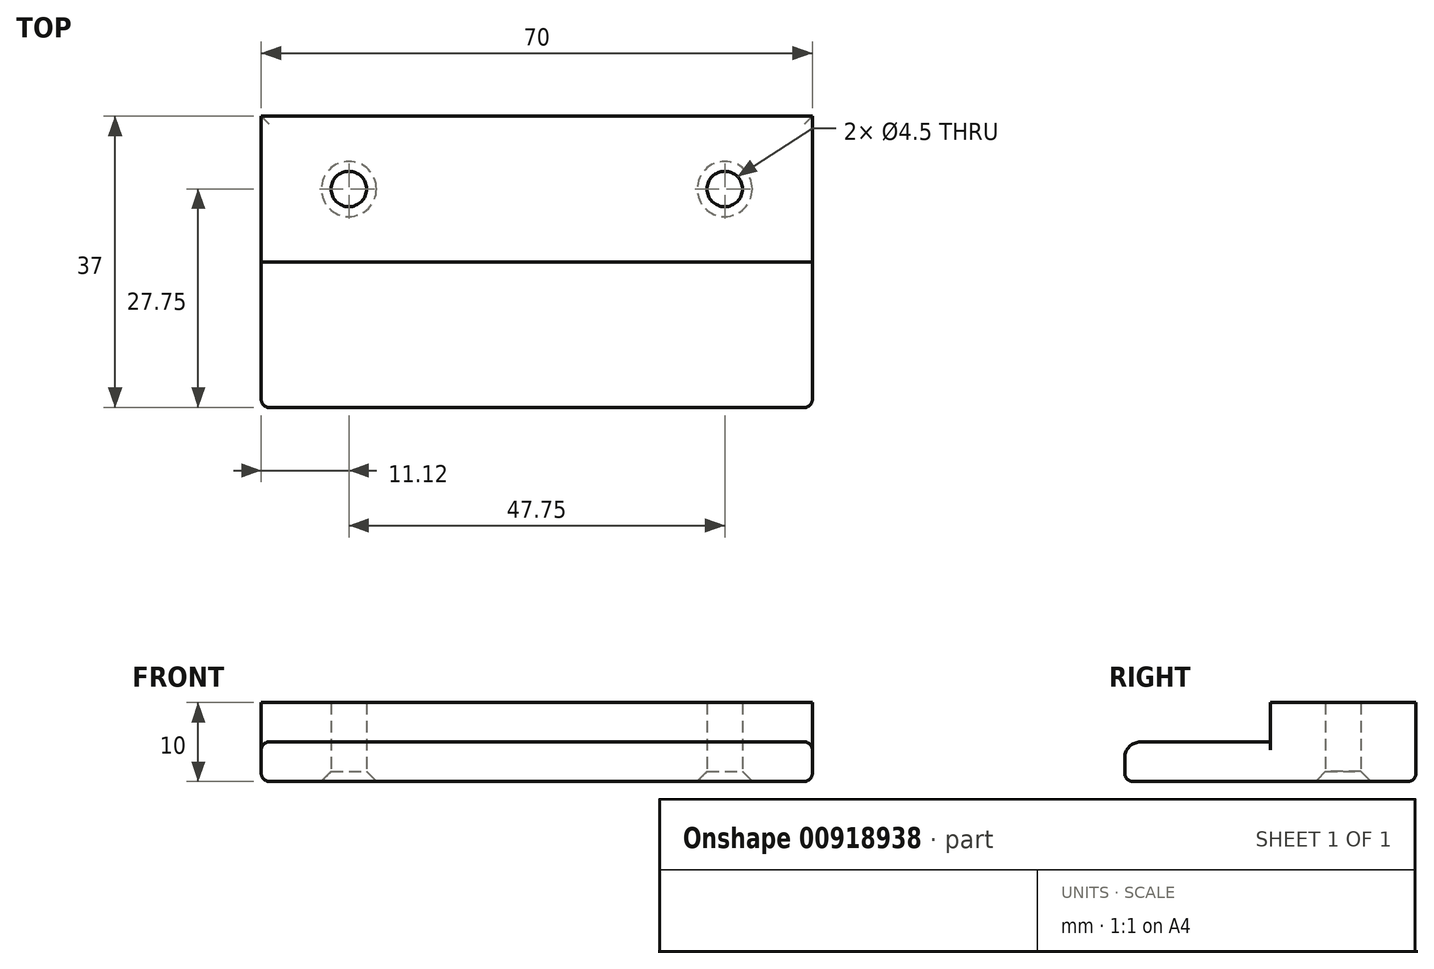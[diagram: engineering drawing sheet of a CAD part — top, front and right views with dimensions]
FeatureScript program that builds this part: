
annotation { "Feature Type Name" : "Feature", "Feature Type Description" : "" }
export const myFeature = defineFeature(function(context is Context, id is Id, definition is map)
    precondition{}
    {
        {
            var Q0;
            Q0=qCreatedBy(makeId("Top.planeOp"),FACE);
            var sketch = newSketch(context, id + "F0", { "sketchPlane" : qUnion([Q0])});
            skLineSegment(sketch, "E0.bottom", {"start": v(-20, 9.25) * mm, "end": v(50, 9.25) * mm});
            skLineSegment(sketch, "E0.top", {"start": v(-20, -9.25) * mm, "end": v(50, -9.25) * mm});
            skLineSegment(sketch, "E0.left", {"start": v(-20, 9.25) * mm, "end": v(-20, -9.25) * mm});
            skLineSegment(sketch, "E0.right", {"start": v(50, 9.25) * mm, "end": v(50, -9.25) * mm});
            skLineSegment(sketch, "E1", {"start": v(15, 9.25) * mm, "end": v(15, -9.25) * mm, "construction": true});
            skLineSegment(sketch, "E2", {"start": v(-20, 0) * mm, "end": v(50, 0) * mm, "construction": true});
            skPoint(sketch, "E2.startSnap0", {"position": v(-20, 0) * mm});
            skPoint(sketch, "E3", {"position": v(-8.87, 0) * mm});
            skPoint(sketch, "E4", {"position": v(38.88, 0) * mm});
            skLineSegment(sketch, "E5", {"start": v(-20, -9.25) * mm, "end": v(-20, -27.75) * mm});
            skLineSegment(sketch, "E6", {"start": v(-20, -27.75) * mm, "end": v(50, -27.75) * mm});
            skLineSegment(sketch, "E7", {"start": v(50, -27.75) * mm, "end": v(50, -9.25) * mm});
            skSolve(sketch);
        }
        {
            var Q0;
            Q0=makeQuery(id+"F0.imprint","IMPRINT",FACE,{"disambiguationData":[TD([[makeQuery(id+"F0.imprint","IMPRINT",EDGE,{"derivedFrom":sQuery(id+"F0.wireOp",EDGE,"E0.bottom")}),-1.0]])]});
            extrude(context, id + "F1", {"entities" : qUnion([Q0]), "depth" : 10 * mm, "offsetDistance" : 25 * mm});
        }
        {
            var Q0;
            Q0=makeQuery(id+"F0.imprint","IMPRINT",FACE,{"disambiguationData":[TD([[makeQuery(id+"F0.imprint","IMPRINT",EDGE,{"derivedFrom":sQuery(id+"F0.wireOp",EDGE,"E0.top")}),-1.0]])]});
            extrude(context, id + "F2", {"entities" : qUnion([Q0]), "operationType" : NewBodyOperationType.ADD, "depth" : 5 * mm, "offsetDistance" : 25 * mm});
        }
        {
            var Q0;
            Q0=makeQuery(id+"F2.opExtrude","CAP_EDGE",EDGE,{"disambiguationData":[OSD([sQuery(id+"F0.wireOp",EDGE,"E6")])],"isStart":false});
            fillet(context, id + "F3", {"entities" : qUnion([Q0]), "radius" : 2 * mm, "tangentPropagation" : true, "allowEdgeOverflow" : false});
        }
        {
            var Q0;
            Q0=makeQuery(id+"F2.opExtrude","CAP_EDGE",EDGE,{"disambiguationData":[OSD([sQuery(id+"F0.wireOp",EDGE,"E7")])],"isStart":false});
            var Q1;
            Q1=makeQuery(id+"F2.opExtrude","CAP_EDGE",EDGE,{"disambiguationData":[OSD([sQuery(id+"F0.wireOp",EDGE,"E5")])],"isStart":false});
            var Q2;
            Q2=makeQuery(id+"F2.boolean.opBoolean","MERGE",EDGE,{"derivedFrom":[makeQuery(id+"F1.opExtrude","CAP_EDGE",EDGE,{"disambiguationData":[OSD([sQuery(id+"F0.wireOp",EDGE,"E0.right")])],"isStart":true}),makeQuery(id+"F2.opExtrude","CAP_EDGE",EDGE,{"disambiguationData":[OSD([sQuery(id+"F0.wireOp",EDGE,"E7")])],"isStart":true})]});
            var Q3;
            Q3=makeQuery(id+"F2.opExtrude","CAP_EDGE",EDGE,{"disambiguationData":[OSD([sQuery(id+"F0.wireOp",EDGE,"E6")])],"isStart":true});
            var Q4;
            Q4=makeQuery(id+"F2.boolean.opBoolean","MERGE",EDGE,{"derivedFrom":[makeQuery(id+"F1.opExtrude","CAP_EDGE",EDGE,{"disambiguationData":[OSD([sQuery(id+"F0.wireOp",EDGE,"E0.left")])],"isStart":true}),makeQuery(id+"F2.opExtrude","CAP_EDGE",EDGE,{"disambiguationData":[OSD([sQuery(id+"F0.wireOp",EDGE,"E5")])],"isStart":true})]});
            var Q5;
            Q5=makeQuery(id+"F1.opExtrude","CAP_EDGE",EDGE,{"disambiguationData":[OSD([sQuery(id+"F0.wireOp",EDGE,"E0.bottom")])],"isStart":true});
            var Q6;
            Q6=makeQuery(id+"F2.opExtrude","CAP_EDGE",EDGE,{"disambiguationData":[OSD([sQuery(id+"F0.wireOp",EDGE,"E0.top")])],"isStart":false});
            fillet(context, id + "F4", {"entities" : qUnion([Q0, Q1, Q2, Q3, Q4, Q5, Q6]), "radius" : 1 * mm, "tangentPropagation" : true, "allowEdgeOverflow" : false});
        }
        {
            var Q0;
            Q0=sQuery(id+"F0.wireOp",VERTEX,"E3");
            var Q1;
            Q1=sQuery(id+"F0.wireOp",VERTEX,"E4");
            var Q2;
            Q2=makeQuery(id+"F1.opExtrude","SWEPT_BODY",BODY,{"disambiguationData":[OSD([sQuery(id+"F0.wireOp",EDGE,"E0.bottom"),sQuery(id+"F0.wireOp",EDGE,"E0.top"),sQuery(id+"F0.wireOp",EDGE,"E0.left"),sQuery(id+"F0.wireOp",EDGE,"E0.right")])]});
            hole(context, id + "F5", {"style" : HoleStyle.C_SINK, "endStyle" : HoleEndStyle.THROUGH, "oppositeDirection" : true, "holeDiameter" : 4.5 * mm, "cSinkDiameter" : 7 * mm, "cSinkAngle" : 90 * degree, "majorDiameter" : 5 * mm, "isTappedThrough" : true, "tappedDepth" : 12 * mm, "tapClearance" : 3, "locations" : qUnion([Q0, Q1]), "scope" : qUnion([Q2])});
        }
    });
